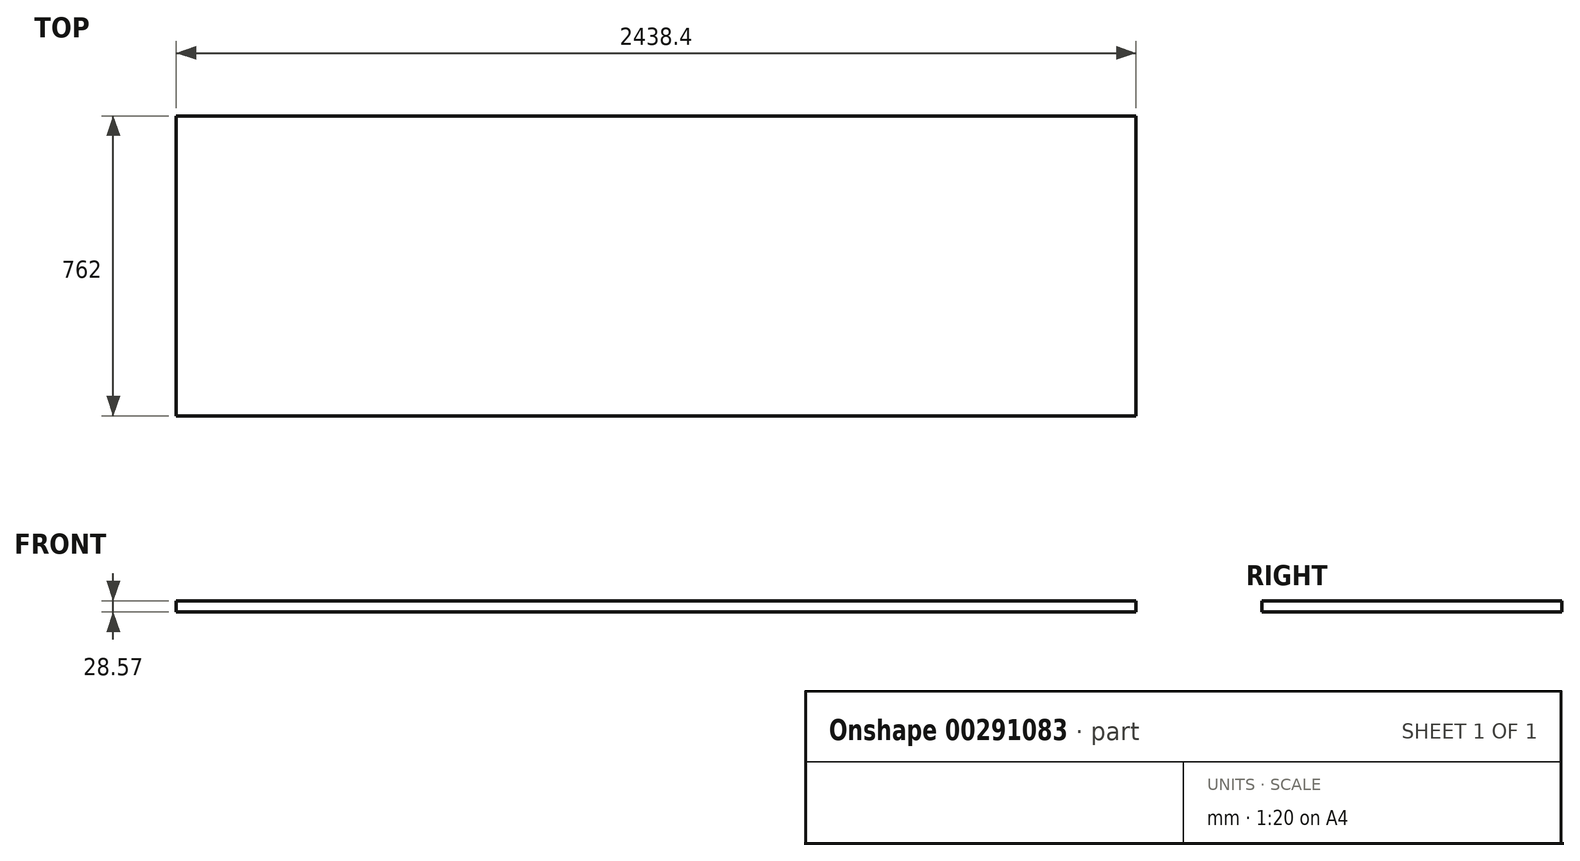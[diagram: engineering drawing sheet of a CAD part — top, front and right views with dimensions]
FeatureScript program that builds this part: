
annotation { "Feature Type Name" : "Feature", "Feature Type Description" : "" }
export const myFeature = defineFeature(function(context is Context, id is Id, definition is map)
    precondition{}
    {
        {
            var Q0;
            Q0=qCreatedBy(makeId("Top.planeOp"),FACE);
            var sketch = newSketch(context, id + "F0", { "sketchPlane" : qUnion([Q0])});
            skLineSegment(sketch, "E0.bottom", {"start": v(0, 0) * mm, "end": v(2438.4, 0) * mm});
            skLineSegment(sketch, "E0.top", {"start": v(0, -762) * mm, "end": v(2438.4, -762) * mm});
            skLineSegment(sketch, "E0.left", {"start": v(0, 0) * mm, "end": v(0, -762) * mm});
            skLineSegment(sketch, "E0.right", {"start": v(2438.4, 0) * mm, "end": v(2438.4, -762) * mm});
            skSolve(sketch);
        }
        {
            var Q0;
            Q0 = qSketchRegion(id + "F0", true);
            extrude(context, id + "F1", {"entities" : qUnion([Q0]), "oppositeDirection" : true, "depth" : 28.57 * mm});
        }
    });
